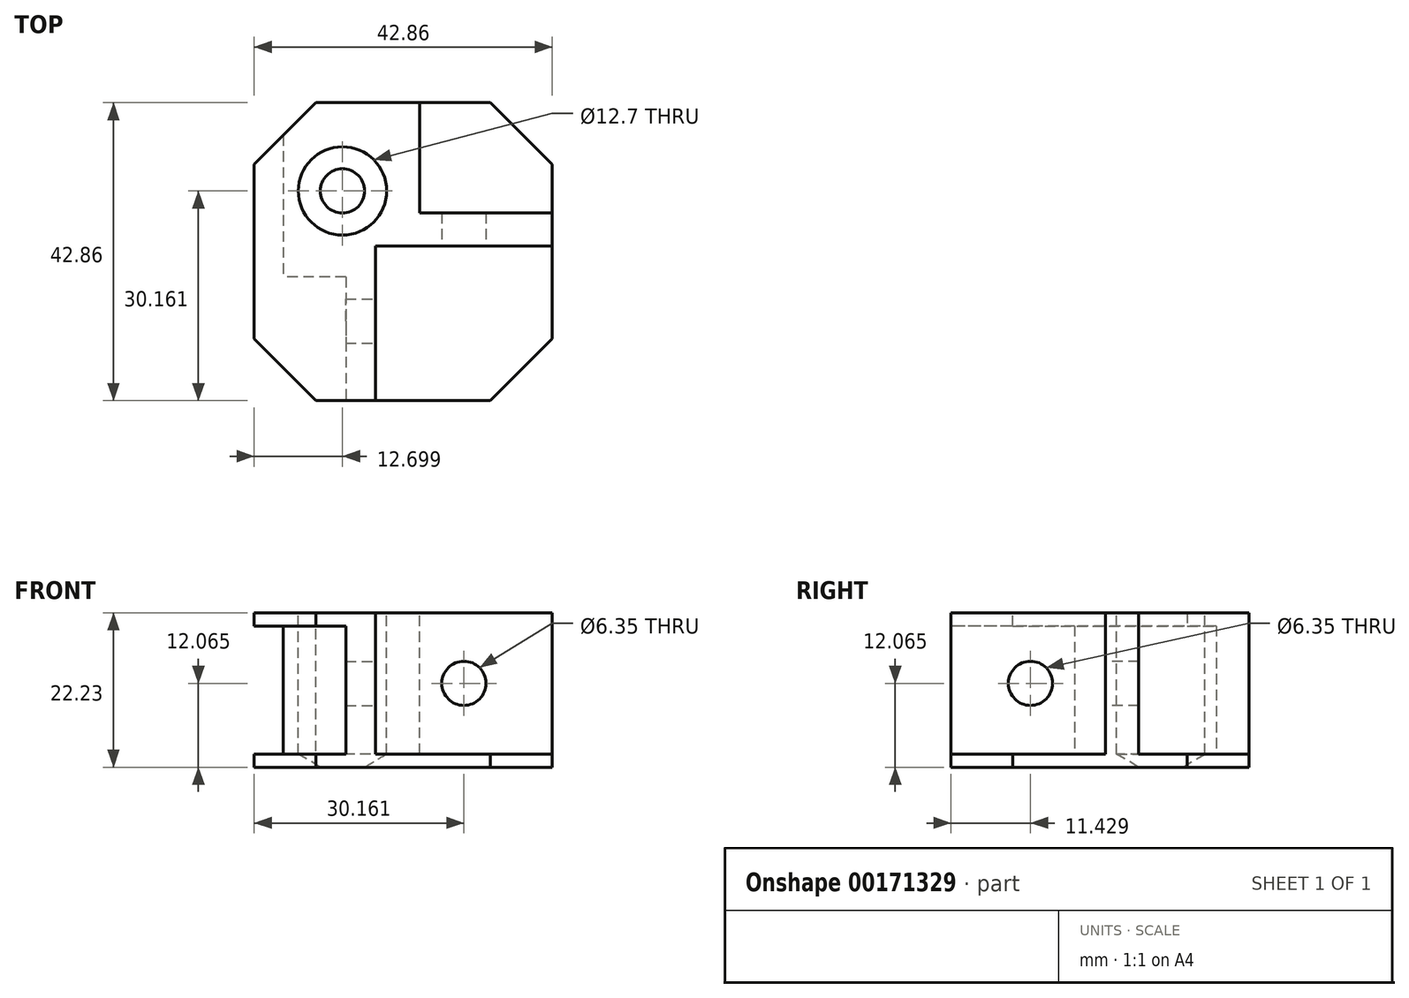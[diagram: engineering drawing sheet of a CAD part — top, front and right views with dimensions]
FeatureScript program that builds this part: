
annotation { "Feature Type Name" : "Feature", "Feature Type Description" : "" }
export const myFeature = defineFeature(function(context is Context, id is Id, definition is map)
    precondition{}
    {
        {
            var Q0;
            Q0=qCreatedBy(makeId("Top.planeOp"),FACE);
            var sketch = newSketch(context, id + "F0", { "sketchPlane" : qUnion([Q0])});
            skLineSegment(sketch, "E0.bottom", {"start": v(21.43, -21.43) * mm, "end": v(-21.43, -21.43) * mm});
            skLineSegment(sketch, "E0.top", {"start": v(21.43, 21.43) * mm, "end": v(-21.43, 21.43) * mm});
            skLineSegment(sketch, "E0.left", {"start": v(21.43, -21.43) * mm, "end": v(21.43, 21.43) * mm});
            skLineSegment(sketch, "E0.right", {"start": v(-21.43, -21.43) * mm, "end": v(-21.43, 21.43) * mm});
            skPoint(sketch, "E0.middle", {"position": v(0, 0) * mm});
            skSolve(sketch);
        }
        {
            var Q0;
            Q0 = qSketchRegion(id + "F0", true);
            extrude(context, id + "F1", {"entities" : qUnion([Q0]), "depth" : 22.22 * mm});
        }
        {
            var Q0;
            Q0=makeQuery(id+"F1.opExtrude","SWEPT_EDGE",EDGE,{"disambiguationData":[OSD([sQuery(id+"F0.wireOp",EDGE,"E0.bottom"),sQuery(id+"F0.wireOp",EDGE,"E0.right")])]});
            var Q1;
            Q1=makeQuery(id+"F1.opExtrude","SWEPT_EDGE",EDGE,{"disambiguationData":[OSD([sQuery(id+"F0.wireOp",EDGE,"E0.bottom"),sQuery(id+"F0.wireOp",EDGE,"E0.left")])]});
            var Q2;
            Q2=makeQuery(id+"F1.opExtrude","SWEPT_EDGE",EDGE,{"disambiguationData":[OSD([sQuery(id+"F0.wireOp",EDGE,"E0.top"),sQuery(id+"F0.wireOp",EDGE,"E0.left")])]});
            var Q3;
            Q3=makeQuery(id+"F1.opExtrude","SWEPT_EDGE",EDGE,{"disambiguationData":[OSD([sQuery(id+"F0.wireOp",EDGE,"E0.top"),sQuery(id+"F0.wireOp",EDGE,"E0.right")])]});
            chamfer(context, id + "F2", {"entities" : qUnion([Q0, Q1, Q2, Q3]), "width" : 8.9 * mm, "tangentPropagation" : true});
        }
        {
            var Q0;
            Q0=makeQuery(id+"F1.opExtrude","CAP_FACE",FACE,{"disambiguationData":[OSD([sQuery(id+"F0.wireOp",EDGE,"E0.bottom"),sQuery(id+"F0.wireOp",EDGE,"E0.top"),sQuery(id+"F0.wireOp",EDGE,"E0.left"),sQuery(id+"F0.wireOp",EDGE,"E0.right")])],"isStart":false});
            var sketch = newSketch(context, id + "F3", { "sketchPlane" : qUnion([Q0])});
            skLineSegment(sketch, "E1.bottom", {"start": v(21.43, -21.43) * mm, "end": v(-3.97, -21.43) * mm});
            skLineSegment(sketch, "E1.top", {"start": v(21.43, 0.8) * mm, "end": v(-3.97, 0.8) * mm});
            skLineSegment(sketch, "E1.left", {"start": v(21.43, -21.43) * mm, "end": v(21.43, 0.8) * mm});
            skLineSegment(sketch, "E1.right", {"start": v(-3.97, -21.43) * mm, "end": v(-3.97, 0.8) * mm});
            skSolve(sketch);
        }
        {
            var Q0;
            Q0 = qSketchRegion(id + "F3", true);
            extrude(context, id + "F4", {"entities" : qUnion([Q0]), "operationType" : NewBodyOperationType.REMOVE, "oppositeDirection" : true, "depth" : 20.32 * mm});
        }
        {
            var Q0;
            Q0=makeQuery(id+"F1.opExtrude","CAP_FACE",FACE,{"disambiguationData":[OSD([sQuery(id+"F0.wireOp",EDGE,"E0.bottom"),sQuery(id+"F0.wireOp",EDGE,"E0.top"),sQuery(id+"F0.wireOp",EDGE,"E0.left"),sQuery(id+"F0.wireOp",EDGE,"E0.right")])],"isStart":false});
            var sketch = newSketch(context, id + "F5", { "sketchPlane" : qUnion([Q0])});
            skLineSegment(sketch, "E2.bottom", {"start": v(2.38, 5.56) * mm, "end": v(21.43, 5.56) * mm});
            skLineSegment(sketch, "E2.top", {"start": v(2.38, 21.43) * mm, "end": v(21.43, 21.43) * mm});
            skLineSegment(sketch, "E2.left", {"start": v(2.38, 5.56) * mm, "end": v(2.38, 21.43) * mm});
            skLineSegment(sketch, "E2.right", {"start": v(21.43, 5.56) * mm, "end": v(21.43, 21.43) * mm});
            skSolve(sketch);
        }
        {
            var Q0;
            Q0 = qSketchRegion(id + "F5", true);
            extrude(context, id + "F6", {"entities" : qUnion([Q0]), "operationType" : NewBodyOperationType.REMOVE, "oppositeDirection" : true, "depth" : 20.32 * mm});
        }
        {
            var Q0;
            {var subQ8=sQuery(id+"F3.wireOp",EDGE,"E1.top");Q0=makeQuery(id+"F3.imprint","IMPRINT",FACE,{"disambiguationData":[TD([[makeQuery(id+"F3.imprint","IMPRINT",EDGE,{"derivedFrom":subQ8}),-1.0]])]});}
            var sketch = newSketch(context, id + "F7", { "sketchPlane" : qUnion([Q0])});
            skPoint(sketch, "E3", {"position": v(-8.73, 8.73) * mm});
            skSolve(sketch);
        }
        {
            var Q0;
            Q0=sQuery(id+"F7.wireOp",VERTEX,"E3");
            var Q1;
            Q1=makeQuery(id+"F1.opExtrude","SWEPT_BODY",BODY,{"disambiguationData":[OSD([sQuery(id+"F0.wireOp",EDGE,"E0.bottom"),sQuery(id+"F0.wireOp",EDGE,"E0.top"),sQuery(id+"F0.wireOp",EDGE,"E0.left"),sQuery(id+"F0.wireOp",EDGE,"E0.right")])]});
            hole(context, id + "F8", {"style" : HoleStyle.SIMPLE, "endStyle" : HoleEndStyle.BLIND, "holeDiameter" : 12.7 * mm, "holeDepth" : 20.32 * mm, "locations" : qUnion([Q0]), "scope" : qUnion([Q1])});
        }
        {
            var Q0;
            Q0=makeQuery(id+"F1.opExtrude","SWEPT_FACE",FACE,{"disambiguationData":[OSD([sQuery(id+"F0.wireOp",EDGE,"E0.bottom")])]});
            var sketch = newSketch(context, id + "F9", { "sketchPlane" : qUnion([Q0])});
            skPoint(sketch, "E4.firstSnap0", {"position": v(-8.26, 22.23) * mm});
            skLineSegment(sketch, "E4.bottom", {"start": v(-8.26, 20.32) * mm, "end": v(-22.44, 20.32) * mm});
            skLineSegment(sketch, "E4.top", {"start": v(-8.26, 1.9) * mm, "end": v(-22.44, 1.9) * mm});
            skLineSegment(sketch, "E4.left", {"start": v(-8.26, 20.32) * mm, "end": v(-8.26, 1.9) * mm});
            skLineSegment(sketch, "E4.right", {"start": v(-22.44, 20.32) * mm, "end": v(-22.44, 1.9) * mm});
            skSolve(sketch);
        }
        {
            var Q0;
            Q0 = qSketchRegion(id + "F9", true);
            extrude(context, id + "F10", {"entities" : qUnion([Q0]), "operationType" : NewBodyOperationType.REMOVE, "oppositeDirection" : true, "depth" : 17.78 * mm});
        }
        {
            var Q0;
            Q0=makeQuery(id+"F10.boolean.opBoolean","COPY",FACE,{"derivedFrom":makeQuery(id+"F10.opExtrude","CAP_FACE",FACE,{"disambiguationData":[OSD([sQuery(id+"F9.wireOp",EDGE,"E4.bottom"),sQuery(id+"F9.wireOp",EDGE,"E4.top"),sQuery(id+"F9.wireOp",EDGE,"E4.left"),sQuery(id+"F9.wireOp",EDGE,"E4.right")])],"isStart":false})});
            var sketch = newSketch(context, id + "F11", { "sketchPlane" : qUnion([Q0])});
            skLineSegment(sketch, "E5.bottom", {"start": v(-17.24, 1.9) * mm, "end": v(-23.5, 1.9) * mm});
            skLineSegment(sketch, "E5.top", {"start": v(-17.24, 20.32) * mm, "end": v(-23.5, 20.32) * mm});
            skLineSegment(sketch, "E5.left", {"start": v(-17.24, 1.9) * mm, "end": v(-17.24, 20.32) * mm});
            skLineSegment(sketch, "E5.right", {"start": v(-23.5, 1.9) * mm, "end": v(-23.5, 20.32) * mm});
            skSolve(sketch);
        }
        {
            var Q0;
            Q0 = qSketchRegion(id + "F11", true);
            extrude(context, id + "F12", {"entities" : qUnion([Q0]), "operationType" : NewBodyOperationType.REMOVE, "endBound" : BoundingType.THROUGH_ALL, "oppositeDirection" : true, "depth" : 25.4 * mm});
        }
        {
            var Q0;
            Q0=makeQuery(id+"F4.boolean.opBoolean","COPY",FACE,{"derivedFrom":makeQuery(id+"F4.opExtrude","SWEPT_FACE",FACE,{"disambiguationData":[OSD([sQuery(id+"F3.wireOp",EDGE,"E1.right")])]})});
            var sketch = newSketch(context, id + "F13", { "sketchPlane" : qUnion([Q0])});
            skPoint(sketch, "E6", {"position": v(-10, 12.06) * mm});
            skSolve(sketch);
        }
        {
            var Q0;
            Q0=sQuery(id+"F13.wireOp",VERTEX,"E6");
            var Q1;
            Q1=makeQuery(id+"F1.opExtrude","SWEPT_BODY",BODY,{"disambiguationData":[OSD([sQuery(id+"F0.wireOp",EDGE,"E0.bottom"),sQuery(id+"F0.wireOp",EDGE,"E0.top"),sQuery(id+"F0.wireOp",EDGE,"E0.left"),sQuery(id+"F0.wireOp",EDGE,"E0.right")])]});
            hole(context, id + "F14", {"style" : HoleStyle.SIMPLE, "endStyle" : HoleEndStyle.THROUGH, "holeDiameter" : 6.35 * mm, "locations" : qUnion([Q0]), "scope" : qUnion([Q1]), "isTappedThrough" : true});
        }
        {
            var Q0;
            Q0=makeQuery(id+"F4.boolean.opBoolean","COPY",FACE,{"derivedFrom":makeQuery(id+"F4.opExtrude","SWEPT_FACE",FACE,{"disambiguationData":[OSD([sQuery(id+"F3.wireOp",EDGE,"E1.top")])]})});
            var sketch = newSketch(context, id + "F15", { "sketchPlane" : qUnion([Q0])});
            skPoint(sketch, "E7", {"position": v(8.73, 12.06) * mm});
            skSolve(sketch);
        }
        {
            var Q0;
            Q0=sQuery(id+"F15.wireOp",VERTEX,"E7");
            var Q1;
            Q1=makeQuery(id+"F1.opExtrude","SWEPT_BODY",BODY,{"disambiguationData":[OSD([sQuery(id+"F0.wireOp",EDGE,"E0.bottom"),sQuery(id+"F0.wireOp",EDGE,"E0.top"),sQuery(id+"F0.wireOp",EDGE,"E0.left"),sQuery(id+"F0.wireOp",EDGE,"E0.right")])]});
            hole(context, id + "F16", {"style" : HoleStyle.SIMPLE, "endStyle" : HoleEndStyle.THROUGH, "holeDiameter" : 6.35 * mm, "locations" : qUnion([Q0]), "scope" : qUnion([Q1]), "isTappedThrough" : true});
        }
    });
